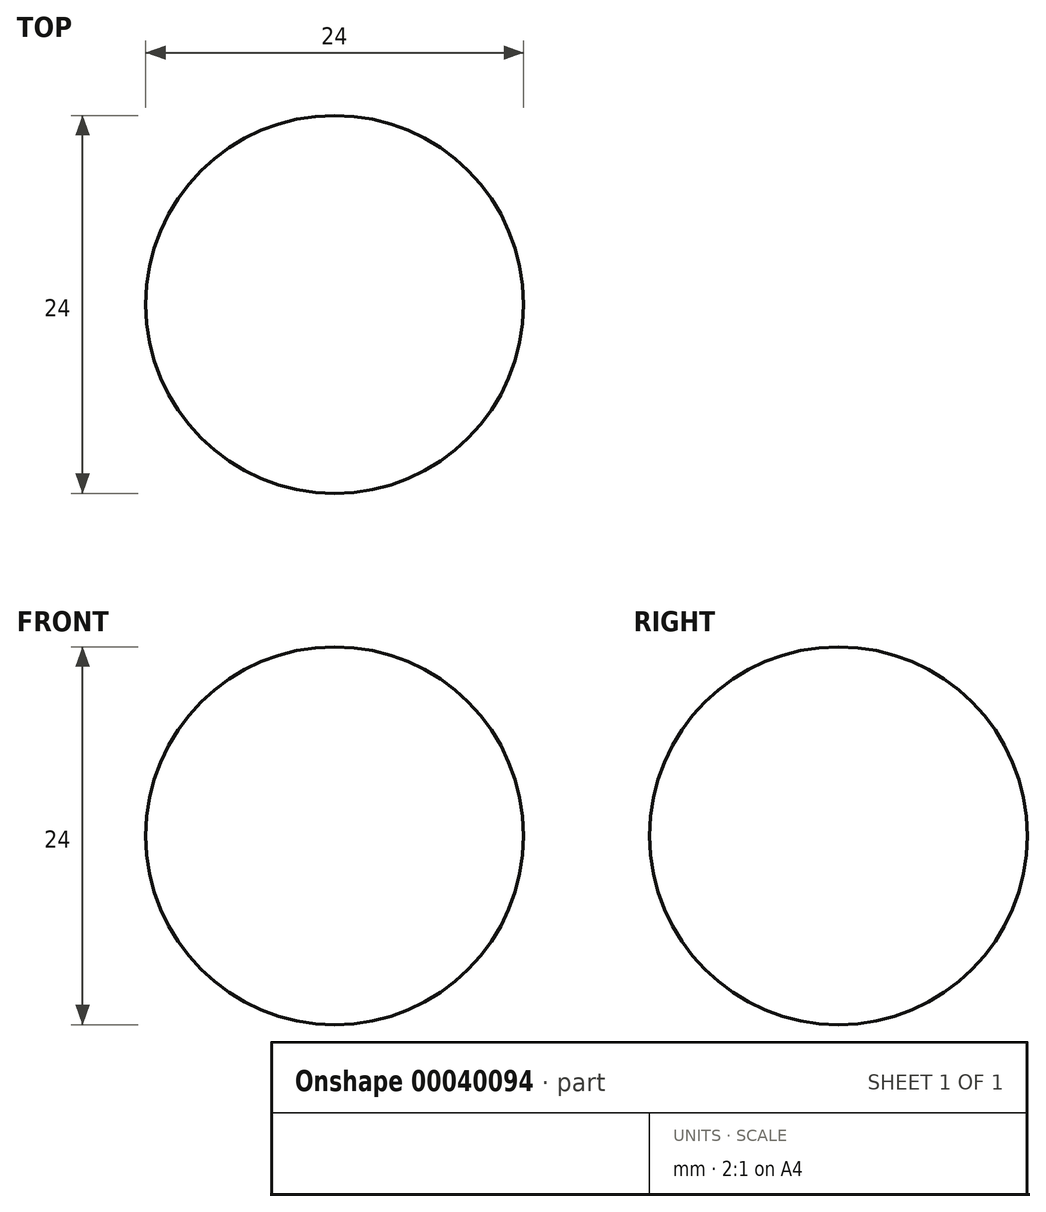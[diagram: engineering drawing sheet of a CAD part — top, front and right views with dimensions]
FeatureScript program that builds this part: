
annotation { "Feature Type Name" : "Feature", "Feature Type Description" : "" }
export const myFeature = defineFeature(function(context is Context, id is Id, definition is map)
    precondition{}
    {
        {
            var Q0;
            Q0=qCreatedBy(makeId("Front.planeOp"),FACE);
            var sketch = newSketch(context, id + "F0", { "sketchPlane" : qUnion([Q0])});
            skArc(sketch, "E0", {"start": v(0, -12) * mm, "mid": v(12, 0) * mm, "end": v(0, 12) * mm});
            skLineSegment(sketch, "E1", {"start": v(0, 12) * mm, "end": v(0, -12) * mm});
            skSolve(sketch);
        }
        {
            var Q0;
            Q0=makeQuery(id+"F0.imprint","IMPRINT",FACE,{"disambiguationData":[TD([[makeQuery(id+"F0.imprint","IMPRINT",EDGE,{"derivedFrom":sQuery(id+"F0.wireOp",EDGE,"E0")}),1.0]])]});
            var Q1;
            Q1=sQuery(id+"F0.wireOp",EDGE,"E1");
            revolve(context, id + "F1", {"entities" : qUnion([Q0]), "axis" : qUnion([Q1]), "revolveType" : RevolveType.FULL});
        }
    });
